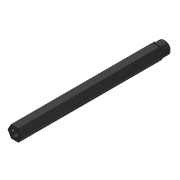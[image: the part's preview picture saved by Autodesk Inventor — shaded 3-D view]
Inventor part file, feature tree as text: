
AUTODESK INVENTOR PART (.ipt)
format: ipt  version: 2013 (Build 170138000, 138)  size: 93,696 bytes
history: native  units: in
note: dims shown in document units (in); Inventor stores cm internally (conversion verified against a paired STEP export)
features: chamfer x1, other x1, hole x1, imported_body x1, sketch x1
ambient origin geometry x8: Origin, YZ Plane, XZ Plane, XY Plane, X Axis, Y Axis, Z Axis, Center Point
feature tree (5):
  chamfer  "Chamfer1"  [1 undecoded]
  other  "217-2617-003 Rev11"
  hole  "Hole1"  [1 undecoded]
  imported_body  "Base1"
  sketch  "Sketch1"  dims[d0=0.25in d1=0.75in d2=0.375in d3=0.25in d4=0.5635in d5=3.0in d6=0.8108in]
note: 2 required parameter values undecoded (feature->parameter linkage not recoverable at this tier; creation-order binding heuristic only, values carry confidence <= 0.55)
